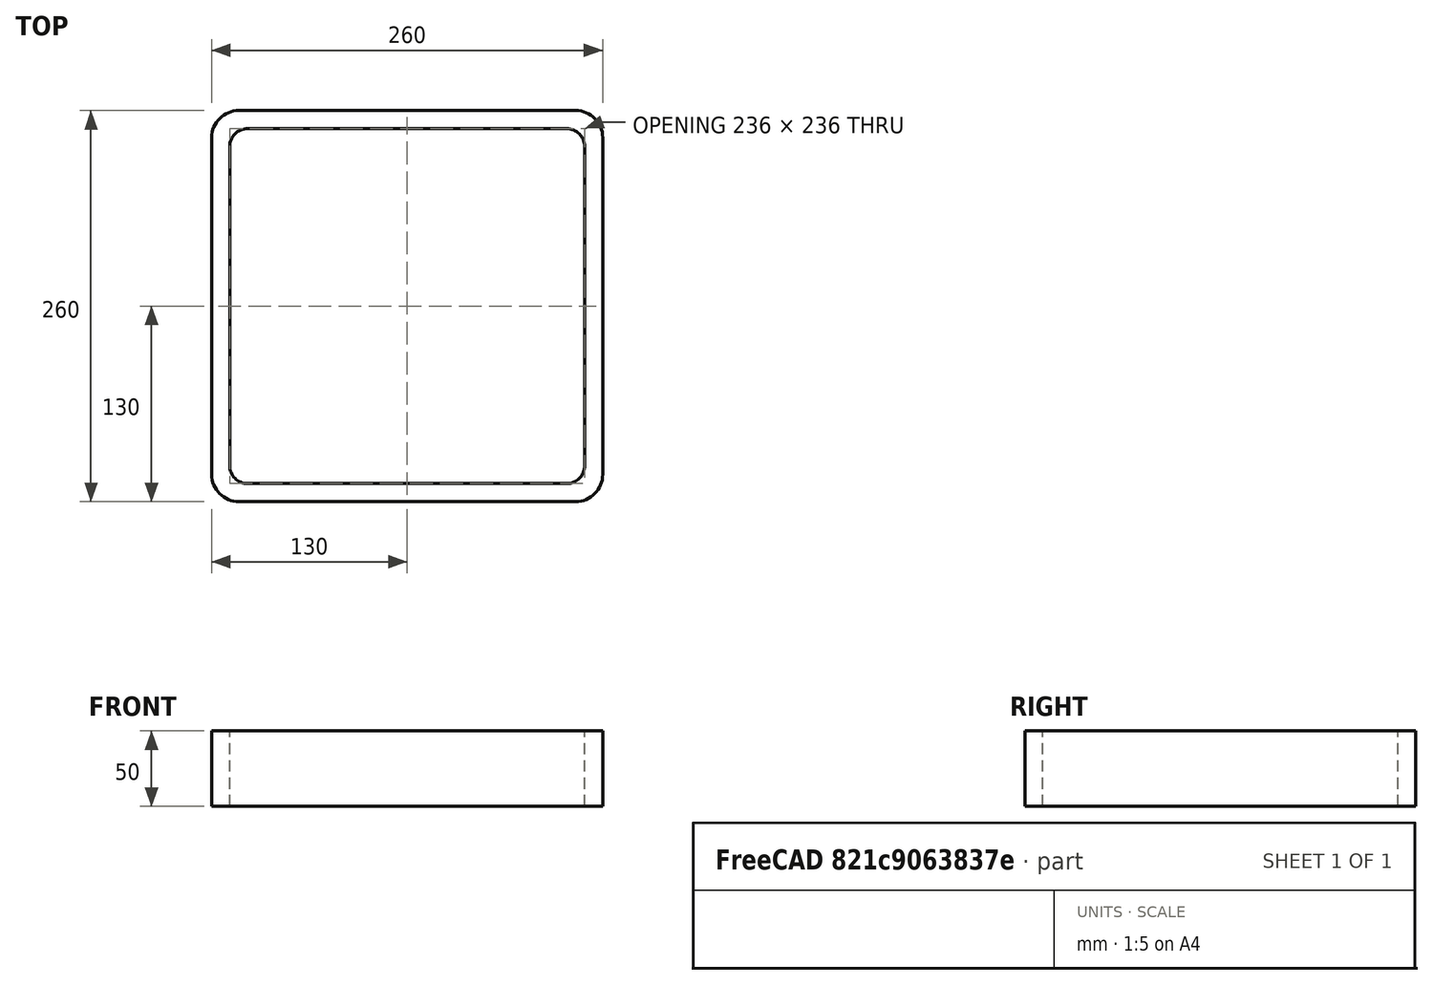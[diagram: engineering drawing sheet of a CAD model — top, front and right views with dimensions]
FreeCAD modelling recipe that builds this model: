
FCSTD DOCUMENT  (FreeCAD 0.15R4671 (Git))
Label: Square hollow section 260x260x12 EN10219 S235JRH
License: All rights reserved
LicenseURL: http://en.wikipedia.org/wiki/All_rights_reserved
objects: Sketcher::SketchObject×1, Part::Extrusion×1
note: 2 computed .brp shape members not serialized (recipe doc carries the construction recipe); baked Part::Feature solids carry a one-line shape summary decoded from their .brp

FEATURE [Sketcher::SketchObject] Sketch
  sketch-geometry (16):
    g0: LineSegment StartX=-106 StartY=118 StartZ=0 EndX=106 EndY=118 EndZ=0
    g1: LineSegment StartX=118 StartY=106 StartZ=0 EndX=118 EndY=-106 EndZ=0
    g2: LineSegment StartX=106 StartY=-118 StartZ=0 EndX=-106 EndY=-118 EndZ=0
    g3: LineSegment StartX=-118 StartY=-106 StartZ=0 EndX=-118 EndY=106 EndZ=0
    g4: LineSegment StartX=-112 StartY=130 StartZ=0 EndX=112 EndY=130 EndZ=0
    g5: LineSegment StartX=130 StartY=112 StartZ=0 EndX=130 EndY=-112 EndZ=0
    g6: LineSegment StartX=112 StartY=-130 StartZ=0 EndX=-112 EndY=-130 EndZ=0
    g7: LineSegment StartX=-130 StartY=-112 StartZ=0 EndX=-130 EndY=112 EndZ=0
    g8: ArcOfCircle CenterX=-106 CenterY=106 CenterZ=0 NormalX=0 NormalY=0 NormalZ=1 Radius=12 StartAngle=1.5708 EndAngle=3.14159
    g9: ArcOfCircle CenterX=106 CenterY=106 CenterZ=0 NormalX=0 NormalY=0 NormalZ=1 Radius=12 StartAngle=0 EndAngle=1.5708
    g10: ArcOfCircle CenterX=106 CenterY=-106 CenterZ=0 NormalX=0 NormalY=0 NormalZ=1 Radius=12 StartAngle=4.71239 EndAngle=6.28319
    g11: ArcOfCircle CenterX=-106 CenterY=-106 CenterZ=0 NormalX=0 NormalY=0 NormalZ=1 Radius=12 StartAngle=3.14159 EndAngle=4.71239
    g12: ArcOfCircle CenterX=112 CenterY=112 CenterZ=0 NormalX=0 NormalY=0 NormalZ=1 Radius=18 StartAngle=0 EndAngle=1.5708
    g13: ArcOfCircle CenterX=112 CenterY=-112 CenterZ=0 NormalX=0 NormalY=0 NormalZ=1 Radius=18 StartAngle=4.71239 EndAngle=6.28319
    g14: ArcOfCircle CenterX=-112 CenterY=-112 CenterZ=0 NormalX=0 NormalY=0 NormalZ=1 Radius=18 StartAngle=3.14159 EndAngle=4.71239
    g15: ArcOfCircle CenterX=-112 CenterY=112 CenterZ=0 NormalX=0 NormalY=0 NormalZ=1 Radius=18 StartAngle=1.5708 EndAngle=3.14159
  constraints (36):
    c: Horizontal(g2)
    c: Vertical(g3)
    c: Horizontal(g6)
    c: Vertical(g7)
    c: Tangent(g3,g8) = 1.5708
    c: Tangent(g0,g8) = 1.5708
    c: Tangent(g0,g9) = 1.5708
    c: Tangent(g1,g9) = 1.5708
    c: Tangent(g1,g10) = 1.5708
    c: Tangent(g2,g10) = 1.5708
    c: Tangent(g2,g11) = 1.5708
    c: Tangent(g3,g11) = 1.5708
    c: Tangent(g4,g12) = 1.5708
    c: Tangent(g5,g12) = 1.5708
    c: Tangent(g5,g13) = 1.5708
    c: Tangent(g6,g13) = 1.5708
    c: Tangent(g6,g14) = 1.5708
    c: Tangent(g7,g14) = 1.5708
    c: Tangent(g7,g15) = 1.5708
    c: Tangent(g4,g15) = 1.5708
    c: Equal(g9,g8)
    c: Equal(g9,g11)
    c: Equal(g9,g10)
    c: Equal(g12,g15)
    c: Equal(g12,g14)
    c: Equal(g12,g13)
    c: Symmetric(g4,g6,g-1)
    c: Symmetric(g7,g5,g-2)
    c: DistanceY(g4,g6) = -260
    c: DistanceX(g7,g5) = 260
    c: Symmetric(g3,g1,g-2)
    c: Symmetric(g0,g2,g-1)
    c: DistanceY(g0,g4) = 12
    c: DistanceX(g5,g1) = -12
    c: Radius(g9) = 12
    c: Radius(g12) = 18
FEATURE [Part::Extrusion] Extrude  label="Square hollow section 260x260x12 EN10219 S235JRH"
  Base = -> Sketch
  Dir = (0,0,50)
  Solid = true
